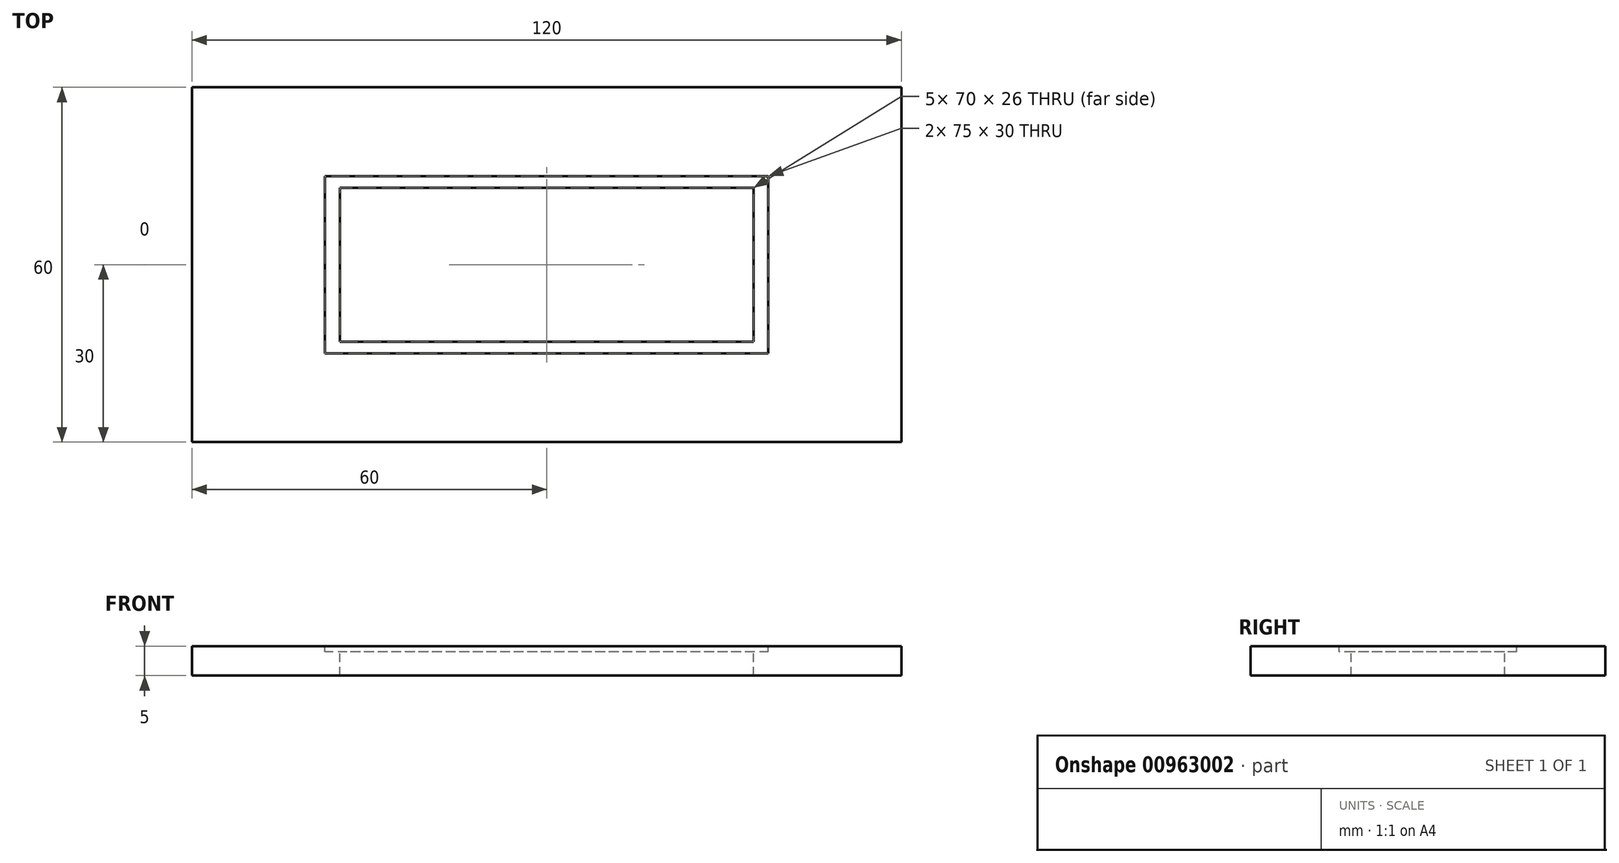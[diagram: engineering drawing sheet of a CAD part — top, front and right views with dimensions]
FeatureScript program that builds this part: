
annotation { "Feature Type Name" : "Feature", "Feature Type Description" : "" }
export const myFeature = defineFeature(function(context is Context, id is Id, definition is map)
    precondition{}
    {
        {
            var Q0;
            Q0=qCreatedBy(makeId("Top.planeOp"),FACE);
            var sketch = newSketch(context, id + "F0", { "sketchPlane" : qUnion([Q0])});
            skLineSegment(sketch, "E0.bottom", {"start": v(60, 30) * mm, "end": v(-60, 30) * mm});
            skLineSegment(sketch, "E0.top", {"start": v(60, -30) * mm, "end": v(-60, -30) * mm});
            skLineSegment(sketch, "E0.left", {"start": v(60, 30) * mm, "end": v(60, -30) * mm});
            skLineSegment(sketch, "E0.right", {"start": v(-60, 30) * mm, "end": v(-60, -30) * mm});
            skPoint(sketch, "E0.middle", {"position": v(0, 0) * mm});
            skSolve(sketch);
        }
        {
            var Q0;
            Q0=qCreatedBy(makeId("Top.planeOp"),FACE);
            var sketch = newSketch(context, id + "F1", { "sketchPlane" : qUnion([Q0])});
            skLineSegment(sketch, "E1.bottom", {"start": v(37.5, 15) * mm, "end": v(-37.5, 15) * mm});
            skLineSegment(sketch, "E1.top", {"start": v(37.5, -15) * mm, "end": v(-37.5, -15) * mm});
            skLineSegment(sketch, "E1.left", {"start": v(37.5, 15) * mm, "end": v(37.5, -15) * mm});
            skLineSegment(sketch, "E1.right", {"start": v(-37.5, 15) * mm, "end": v(-37.5, -15) * mm});
            skPoint(sketch, "E1.middle", {"position": v(0, 0) * mm});
            skSolve(sketch);
        }
        {
            var Q0;
            Q0=qCreatedBy(makeId("Top.planeOp"),FACE);
            var sketch = newSketch(context, id + "F2", { "sketchPlane" : qUnion([Q0])});
            skLineSegment(sketch, "E2.bottom", {"start": v(35, 13) * mm, "end": v(-35, 13) * mm});
            skLineSegment(sketch, "E2.top", {"start": v(35, -13) * mm, "end": v(-35, -13) * mm});
            skLineSegment(sketch, "E2.left", {"start": v(35, 13) * mm, "end": v(35, -13) * mm});
            skLineSegment(sketch, "E2.right", {"start": v(-35, 13) * mm, "end": v(-35, -13) * mm});
            skPoint(sketch, "E2.middle", {"position": v(0, 0) * mm});
            skSolve(sketch);
        }
        {
            var Q0;
            Q0 = qSketchRegion(id + "F0", true);
            extrude(context, id + "F3", {"entities" : qUnion([Q0]), "oppositeDirection" : true, "depth" : 5 * mm, "offsetDistance" : 25 * mm});
        }
        {
            var Q0;
            Q0 = qSketchRegion(id + "F1", true);
            extrude(context, id + "F4", {"entities" : qUnion([Q0]), "operationType" : NewBodyOperationType.REMOVE, "oppositeDirection" : true, "depth" : 1 * mm, "offsetDistance" : 25 * mm});
        }
        {
            var Q0;
            Q0 = qSketchRegion(id + "F2", true);
            extrude(context, id + "F5", {"entities" : qUnion([Q0]), "operationType" : NewBodyOperationType.REMOVE, "oppositeDirection" : true, "depth" : 10 * mm, "offsetDistance" : 25 * mm});
        }
    });
